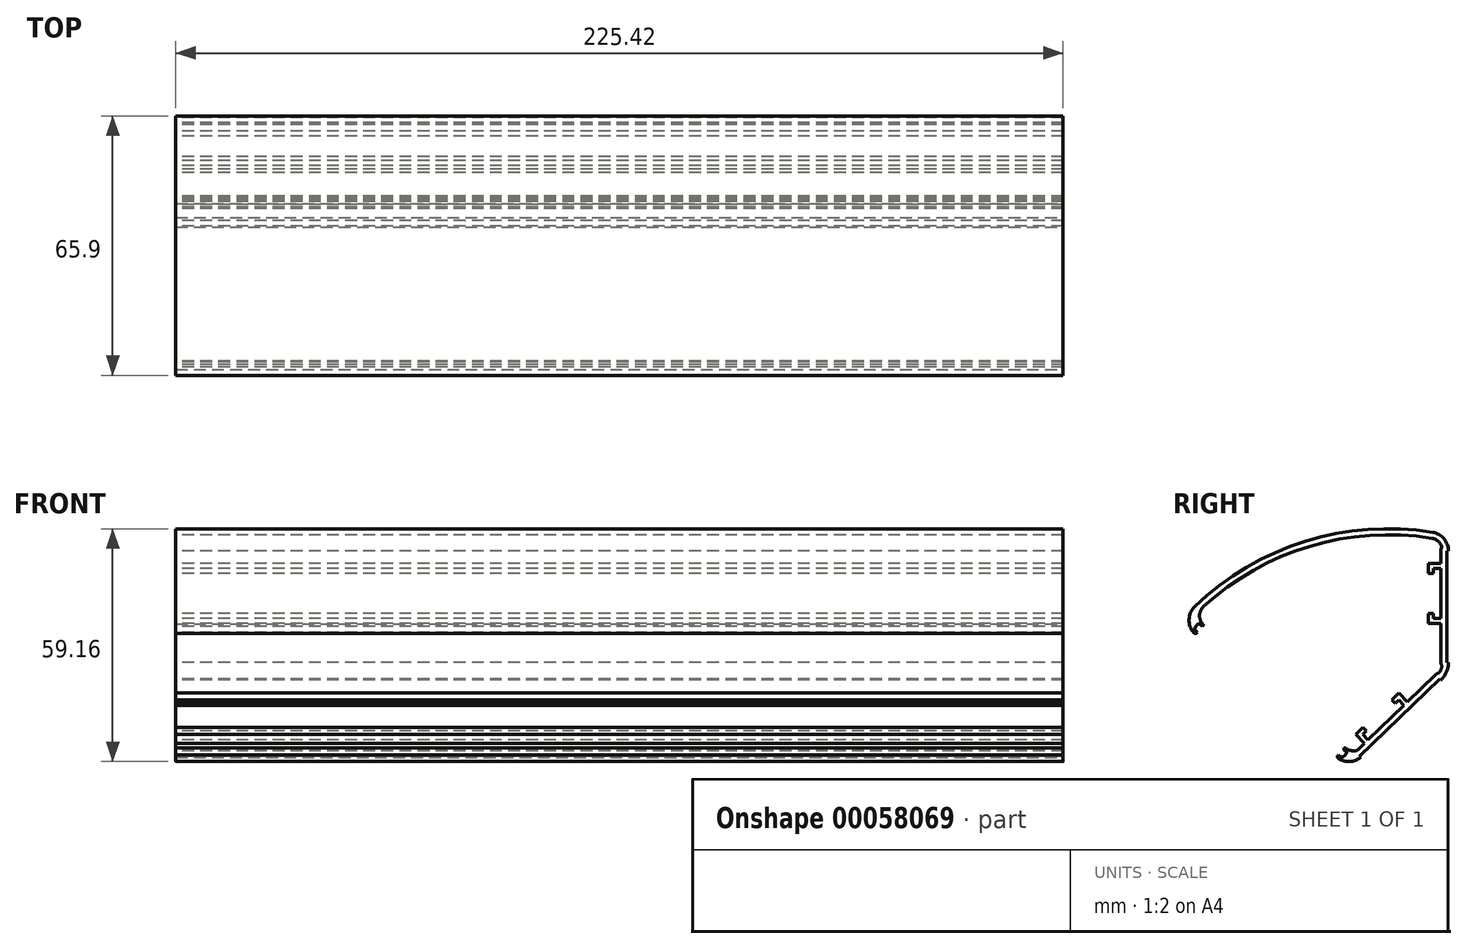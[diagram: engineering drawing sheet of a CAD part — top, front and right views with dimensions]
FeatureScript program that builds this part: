
annotation { "Feature Type Name" : "Feature", "Feature Type Description" : "" }
export const myFeature = defineFeature(function(context is Context, id is Id, definition is map)
    precondition{}
    {
        {
            var Q0;
            Q0=qCreatedBy(makeId("Right.planeOp"),FACE);
            var sketch = newSketch(context, id + "F0", { "sketchPlane" : qUnion([Q0])});
            skLineSegment(sketch, "E0", {"start": v(-25.12, -24.26) * mm, "end": v(0, 0) * mm});
            skLineSegment(sketch, "E1", {"start": v(0, 0) * mm, "end": v(0, 34.93) * mm});
            skArc(sketch, "E2", {"start": v(0, 34.92) * mm, "mid": v(-34.7, 33.87) * mm, "end": v(-64.76, 16.49) * mm});
            skLineSegment(sketch, "E3", {"start": v(-64.76, 16.49) * mm, "end": v(-68.18, 13.16) * mm});
            skLineSegment(sketch, "E4", {"start": v(-25.12, -24.26) * mm, "end": v(-68.18, 13.16) * mm});
            skLineSegment(sketch, "E5", {"start": v(-64.76, 16.49) * mm, "end": v(-25.12, -24.26) * mm, "construction": true});
            skLineSegment(sketch, "E6", {"start": v(-64.76, 16.49) * mm, "end": v(0, 34.93) * mm, "construction": true});
            skSolve(sketch);
        }
        {
            var Q0;
            Q0=qSketchRegion(id+"F0",true);
            extrude(context, id + "F1", {"entities" : qUnion([Q0]), "endBound" : BoundingType.SYMMETRIC, "depth" : 225.42 * mm});
        }
        {
            var Q0;
            Q0=makeQuery(id+"F1.opExtrude","SWEPT_EDGE",EDGE,{"disambiguationData":[OSD([sQuery(id+"F0.wireOp",EDGE,"E1"),sQuery(id+"F0.wireOp",EDGE,"E2")])]});
            var Q1;
            Q1=makeQuery(id+"F1.opExtrude","SWEPT_EDGE",EDGE,{"disambiguationData":[OSD([sQuery(id+"F0.wireOp",EDGE,"E0"),sQuery(id+"F0.wireOp",EDGE,"E4")])]});
            var Q2;
            Q2=makeQuery(id+"F1.opExtrude","SWEPT_EDGE",EDGE,{"disambiguationData":[OSD([sQuery(id+"F0.wireOp",EDGE,"E3"),sQuery(id+"F0.wireOp",EDGE,"E4")])]});
            fillet(context, id + "F2", {"entities" : qUnion([Q0, Q1, Q2]), "radius" : 4.76 * mm, "tangentPropagation" : true, "allowEdgeOverflow" : false});
        }
        {
            var Q0;
            Q0=makeQuery(id+"F1.opExtrude","SWEPT_EDGE",EDGE,{"disambiguationData":[OSD([sQuery(id+"F0.wireOp",EDGE,"E0"),sQuery(id+"F0.wireOp",EDGE,"E1")])]});
            fillet(context, id + "F3", {"entities" : qUnion([Q0]), "radius" : 6.35 * mm, "tangentPropagation" : true, "allowEdgeOverflow" : false});
        }
        {
            var Q0;
            Q0=makeQuery(id+"F1.opExtrude","CAP_FACE",FACE,{"disambiguationData":[OSD([sQuery(id+"F0.wireOp",EDGE,"E0"),sQuery(id+"F0.wireOp",EDGE,"E1"),sQuery(id+"F0.wireOp",EDGE,"E2"),sQuery(id+"F0.wireOp",EDGE,"E3"),sQuery(id+"F0.wireOp",EDGE,"E4")])],"isStart":true});
            var Q1;
            Q1=makeQuery(id+"F1.opExtrude","CAP_FACE",FACE,{"disambiguationData":[OSD([sQuery(id+"F0.wireOp",EDGE,"E0"),sQuery(id+"F0.wireOp",EDGE,"E1"),sQuery(id+"F0.wireOp",EDGE,"E2"),sQuery(id+"F0.wireOp",EDGE,"E3"),sQuery(id+"F0.wireOp",EDGE,"E4")])],"isStart":false});
            var Q2;
            Q2=makeQuery(id+"F1.opExtrude","SWEPT_FACE",FACE,{"disambiguationData":[OSD([sQuery(id+"F0.wireOp",EDGE,"E4")])]});
            shell(context, id + "F4", {"entities" : qUnion([Q0, Q1, Q2]), "thickness" : 1.52 * mm});
        }
        {
            var Q0;
            Q0=makeQuery(id+"F1.opExtrude","CAP_FACE",FACE,{"disambiguationData":[OSD([sQuery(id+"F0.wireOp",EDGE,"E0"),sQuery(id+"F0.wireOp",EDGE,"E1"),sQuery(id+"F0.wireOp",EDGE,"E2"),sQuery(id+"F0.wireOp",EDGE,"E3"),sQuery(id+"F0.wireOp",EDGE,"E4")])],"isStart":true});
            var sketch = newSketch(context, id + "F5", { "sketchPlane" : qUnion([Q0])});
            skLineSegment(sketch, "E7", {"start": v(63.27, 10.92) * mm, "end": v(62.18, 12.16) * mm});
            skArc(sketch, "E8.0", {"start": v(63.27, 10.92) * mm, "mid": v(64.38, 13.28) * mm, "end": v(63.39, 15.7) * mm});
            skArc(sketch, "E9", {"start": v(62.18, 12.16) * mm, "mid": v(63.23, 14.47) * mm, "end": v(62.22, 16.8) * mm});
            skSolve(sketch);
        }
        {
            var Q0;
            {var subQ0=sQuery(id+"F0.wireOp",EDGE,"E3");Q0=makeQuery(id+"FXWxfeTe23RxrKB_1.boolean.opBoolean","MERGE",FACE,{"derivedFrom":[makeQuery(id+"F1.opExtrude","CAP_FACE",FACE,{"disambiguationData":[OSD([sQuery(id+"F0.wireOp",EDGE,"E0"),sQuery(id+"F0.wireOp",EDGE,"E1"),sQuery(id+"F0.wireOp",EDGE,"E2"),subQ0,sQuery(id+"F0.wireOp",EDGE,"E4")])],"isStart":true}),makeQuery(id+"FXWxfeTe23RxrKB_1.opExtrude","CAP_FACE",FACE,{"disambiguationData":[OSD([subQ0,sQuery(id+"F5.wireOp",EDGE,"f8929549-29da-4568-b1ae-587f62ae2228.0"),sQuery(id+"F5.wireOp",EDGE,"E7"),sQuery(id+"F5.wireOp",EDGE,"b0cd2a88-d953-423b-8e6f-4eb86873c5e2")])],"isStart":true})]});}
            var sketch = newSketch(context, id + "F6", { "sketchPlane" : qUnion([Q0])});
            skArc(sketch, "E10.0", {"start": v(23.04, -20.13) * mm, "mid": v(25.2, -21.04) * mm, "end": v(27.42, -20.25) * mm});
            skLineSegment(sketch, "E11", {"start": v(27.42, -20.25) * mm, "end": v(26.33, -19) * mm});
            skArc(sketch, "E12", {"start": v(21.75, -18.88) * mm, "mid": v(24.02, -19.83) * mm, "end": v(26.33, -19) * mm});
            skLineSegment(sketch, "E13", {"start": v(26.33, -19) * mm, "end": v(24.2, -20.85) * mm, "construction": true});
            skSolve(sketch);
        }
        {
            var Q0;
            Q0=makeQuery(id+"F5.imprint","IMPRINT",FACE,{"disambiguationData":[TD([[makeQuery(id+"F5.imprint","IMPRINT",EDGE,{"derivedFrom":sQuery(id+"F5.wireOp",EDGE,"E7")}),-1.0]])]});
            var Q1;
            {var subQ0=sQuery(id+"F6.wireOp",EDGE,"E10.0");Q1=makeQuery(id+"F6.imprint","IMPRINT",FACE,{"disambiguationData":[TD([[makeQuery(id+"F6.imprint","IMPRINT",EDGE,{"derivedFrom":subQ0}),1.0]])]});}
            var Q2;
            Q2=makeQuery(id+"F1.opExtrude","CAP_FACE",FACE,{"disambiguationData":[OSD([sQuery(id+"F0.wireOp",EDGE,"E0"),sQuery(id+"F0.wireOp",EDGE,"E1"),sQuery(id+"F0.wireOp",EDGE,"E2"),sQuery(id+"F0.wireOp",EDGE,"E3"),sQuery(id+"F0.wireOp",EDGE,"E4")])],"isStart":false});
            extrude(context, id + "F7", {"entities" : qUnion([Q0, Q1]), "operationType" : NewBodyOperationType.ADD, "endBound" : BoundingType.UP_TO_SURFACE, "oppositeDirection" : true, "endBoundEntityFace" : qUnion([Q2]), "depth" : 25.4 * mm});
        }
        {
            var Q0;
            {var subQ0=sQuery(id+"F0.wireOp",EDGE,"E0");var subQ1=sQuery(id+"F0.wireOp",EDGE,"E2");Q0=makeQuery(id+"F7.boolean.opBoolean","MERGE",FACE,{"derivedFrom":[makeQuery(id+"F1.opExtrude","CAP_FACE",FACE,{"disambiguationData":[OSD([subQ0,sQuery(id+"F0.wireOp",EDGE,"E1"),subQ1,sQuery(id+"F0.wireOp",EDGE,"E3"),sQuery(id+"F0.wireOp",EDGE,"E4")])],"isStart":true}),makeQuery(id+"F7.opExtrude","CAP_FACE",FACE,{"disambiguationData":[OSD([subQ1,sQuery(id+"F5.wireOp",EDGE,"E7"),sQuery(id+"F5.wireOp",EDGE,"E8.0"),sQuery(id+"F5.wireOp",EDGE,"E9")])],"isStart":true}),makeQuery(id+"F7.opExtrude","CAP_FACE",FACE,{"disambiguationData":[OSD([subQ0,sQuery(id+"F6.wireOp",EDGE,"E10.0"),sQuery(id+"F6.wireOp",EDGE,"E11"),sQuery(id+"F6.wireOp",EDGE,"E12")])],"isStart":true})]});}
            var sketch = newSketch(context, id + "F8", { "sketchPlane" : qUnion([Q0])});
            skLineSegment(sketch, "E14", {"start": v(63.18, 11.01) * mm, "end": v(27.33, -20.15) * mm, "construction": true});
            skSolve(sketch);
        }
        {
            var Q0;
            {var subQ4=sQuery(id+"F0.wireOp",EDGE,"E0");var subQ12=makeQuery(id+"F1.opExtrude","CAP_EDGE",EDGE,{"disambiguationData":[OSD([subQ4])],"isStart":true});Q0=makeQuery(id+"F8.imprint","IMPRINT",FACE,{"disambiguationData":[TD([[makeQuery(id+"F8.imprint","IMPRINT",EDGE,{"derivedFrom":subQ12}),-1.0]])]});}
            var sketch = newSketch(context, id + "F9", { "sketchPlane" : qUnion([Q0])});
            skLineSegment(sketch, "E15", {"start": v(62.56, 11.73) * mm, "end": v(63.8, 10.3) * mm});
            skLineSegment(sketch, "E16", {"start": v(63.8, 10.3) * mm, "end": v(64.77, 11.13) * mm});
            skLineSegment(sketch, "E17", {"start": v(64.77, 11.13) * mm, "end": v(63.52, 12.56) * mm});
            skLineSegment(sketch, "E18", {"start": v(63.52, 12.56) * mm, "end": v(62.56, 11.73) * mm});
            skPoint(sketch, "E19", {"position": v(63.18, 11.01) * mm});
            skSolve(sketch);
        }
        {
            var Q0;
            {var subQ4=sQuery(id+"F0.wireOp",EDGE,"E0");var subQ12=makeQuery(id+"F1.opExtrude","CAP_EDGE",EDGE,{"disambiguationData":[OSD([subQ4])],"isStart":true});Q0=makeQuery(id+"F8.imprint","IMPRINT",FACE,{"disambiguationData":[TD([[makeQuery(id+"F8.imprint","IMPRINT",EDGE,{"derivedFrom":subQ12}),-1.0]])]});}
            var sketch = newSketch(context, id + "F10", { "sketchPlane" : qUnion([Q0])});
            skLineSegment(sketch, "E20", {"start": v(26.7, -19.43) * mm, "end": v(27.96, -20.87) * mm});
            skLineSegment(sketch, "E21", {"start": v(27.96, -20.87) * mm, "end": v(27, -21.7) * mm});
            skLineSegment(sketch, "E22", {"start": v(27, -21.7) * mm, "end": v(25.75, -20.27) * mm});
            skLineSegment(sketch, "E23", {"start": v(25.75, -20.27) * mm, "end": v(26.7, -19.43) * mm});
            skPoint(sketch, "E24", {"position": v(27.33, -20.15) * mm});
            skSolve(sketch);
        }
        {
            var Q0;
            Q0 = qSketchRegion(id + "F9", true);
            var Q1;
            Q1 = qSketchRegion(id + "F10", true);
            var Q2;
            {var subQ0=sQuery(id+"F0.wireOp",EDGE,"E0");var subQ1=sQuery(id+"F0.wireOp",EDGE,"E2");Q2=makeQuery(id+"F7.boolean.opBoolean","MERGE",FACE,{"derivedFrom":[makeQuery(id+"F1.opExtrude","CAP_FACE",FACE,{"disambiguationData":[OSD([subQ0,sQuery(id+"F0.wireOp",EDGE,"E1"),subQ1,sQuery(id+"F0.wireOp",EDGE,"E3"),sQuery(id+"F0.wireOp",EDGE,"E4")])],"isStart":false}),makeQuery(id+"F7.opExtrude","CAP_FACE",FACE,{"disambiguationData":[OSD([subQ1,sQuery(id+"F5.wireOp",EDGE,"E7"),sQuery(id+"F5.wireOp",EDGE,"E8.0"),sQuery(id+"F5.wireOp",EDGE,"E9")])],"isStart":false}),makeQuery(id+"F7.opExtrude","CAP_FACE",FACE,{"disambiguationData":[OSD([subQ0,sQuery(id+"F6.wireOp",EDGE,"E10.0"),sQuery(id+"F6.wireOp",EDGE,"E11"),sQuery(id+"F6.wireOp",EDGE,"E12")])],"isStart":false})]});}
            extrude(context, id + "F11", {"entities" : qUnion([Q0, Q1]), "operationType" : NewBodyOperationType.REMOVE, "endBound" : BoundingType.UP_TO_SURFACE, "oppositeDirection" : true, "endBoundEntityFace" : qUnion([Q2]), "depth" : 25.4 * mm});
        }
        {
            var Q0;
            Q0=makeQuery(id+"F11.boolean.opBoolean","COPY",EDGE,{"derivedFrom":makeQuery(id+"F11.opExtrude","SWEPT_EDGE",EDGE,{"disambiguationData":[OSD([sQuery(id+"F10.wireOp",EDGE,"E21"),sQuery(id+"F10.wireOp",EDGE,"E22")])]})});
            var Q1;
            Q1=makeQuery(id+"F11.boolean.opBoolean","COPY",EDGE,{"derivedFrom":makeQuery(id+"F11.opExtrude","SWEPT_EDGE",EDGE,{"disambiguationData":[OSD([sQuery(id+"F9.wireOp",EDGE,"E16"),sQuery(id+"F9.wireOp",EDGE,"E17")])]})});
            fillet(context, id + "F12", {"entities" : qUnion([Q0, Q1]), "radius" : 0.76 * mm, "tangentPropagation" : true, "allowEdgeOverflow" : false});
        }
        {
            var Q0;
            {var subQ0=sQuery(id+"F0.wireOp",EDGE,"E4");Q0=makeQuery(id+"F2.opFillet","BLEND_EDGE",EDGE,{"blendedFrom":[makeQuery(id+"F1.opExtrude","SWEPT_EDGE",EDGE,{"disambiguationData":[OSD([sQuery(id+"F0.wireOp",EDGE,"E3"),subQ0])]}),makeQuery(id+"F1.opExtrude","SWEPT_FACE",FACE,{"disambiguationData":[OSD([subQ0])]})],"blendedInto":[makeQuery(id+"F1.opExtrude","SWEPT_FACE",FACE,{"disambiguationData":[OSD([subQ0])]})]});}
            var Q1;
            {var subQ0=sQuery(id+"F0.wireOp",EDGE,"E4");Q1=makeQuery(id+"F2.opFillet","BLEND_EDGE",EDGE,{"blendedFrom":[makeQuery(id+"F1.opExtrude","SWEPT_EDGE",EDGE,{"disambiguationData":[OSD([sQuery(id+"F0.wireOp",EDGE,"E0"),subQ0])]}),makeQuery(id+"F1.opExtrude","SWEPT_FACE",FACE,{"disambiguationData":[OSD([subQ0])]})],"blendedInto":[makeQuery(id+"F1.opExtrude","SWEPT_FACE",FACE,{"disambiguationData":[OSD([subQ0])]})]});}
            fillet(context, id + "F13", {"entities" : qUnion([Q0, Q1]), "radius" : 0.5 * mm, "tangentPropagation" : true, "allowEdgeOverflow" : false});
        }
        {
            var Q0;
            Q0=makeQuery(id+"F11.boolean.opBoolean","COPY",EDGE,{"derivedFrom":makeQuery(id+"F11.opExtrude","SWEPT_EDGE",EDGE,{"disambiguationData":[OSD([sQuery(id+"F10.wireOp",EDGE,"E22"),sQuery(id+"F10.wireOp",EDGE,"E23")])]})});
            var Q1;
            Q1=makeQuery(id+"F11.boolean.opBoolean","COPY",EDGE,{"derivedFrom":makeQuery(id+"F11.opExtrude","SWEPT_EDGE",EDGE,{"disambiguationData":[OSD([sQuery(id+"F0.wireOp",EDGE,"E0"),sQuery(id+"F0.wireOp",EDGE,"E1"),sQuery(id+"F0.wireOp",EDGE,"E2"),sQuery(id+"F0.wireOp",EDGE,"E3"),sQuery(id+"F0.wireOp",EDGE,"E4"),sQuery(id+"F6.wireOp",EDGE,"E11"),sQuery(id+"F10.wireOp",EDGE,"E20"),sQuery(id+"F10.wireOp",EDGE,"E23")])]})});
            var Q2;
            Q2=makeQuery(id+"F7.opExtrude","SWEPT_EDGE",EDGE,{"disambiguationData":[OSD([sQuery(id+"F6.wireOp",EDGE,"E11"),sQuery(id+"F6.wireOp",EDGE,"E12")])]});
            var Q3;
            Q3=makeQuery(id+"F11.boolean.opBoolean","COPY",EDGE,{"derivedFrom":makeQuery(id+"F11.opExtrude","SWEPT_EDGE",EDGE,{"disambiguationData":[OSD([sQuery(id+"F0.wireOp",EDGE,"E0"),sQuery(id+"F0.wireOp",EDGE,"E1"),sQuery(id+"F0.wireOp",EDGE,"E2"),sQuery(id+"F0.wireOp",EDGE,"E3"),sQuery(id+"F0.wireOp",EDGE,"E4"),sQuery(id+"F5.wireOp",EDGE,"E7"),sQuery(id+"F9.wireOp",EDGE,"E15"),sQuery(id+"F9.wireOp",EDGE,"E18")])]})});
            var Q4;
            Q4=makeQuery(id+"F7.opExtrude","SWEPT_EDGE",EDGE,{"disambiguationData":[OSD([sQuery(id+"F5.wireOp",EDGE,"E7"),sQuery(id+"F5.wireOp",EDGE,"E9")])]});
            var Q5;
            Q5=makeQuery(id+"F11.boolean.opBoolean","COPY",EDGE,{"derivedFrom":makeQuery(id+"F11.opExtrude","SWEPT_EDGE",EDGE,{"disambiguationData":[OSD([sQuery(id+"F9.wireOp",EDGE,"E17"),sQuery(id+"F9.wireOp",EDGE,"E18")])]})});
            fillet(context, id + "F14", {"entities" : qUnion([Q0, Q1, Q2, Q3, Q4, Q5]), "radius" : 0.25 * mm, "tangentPropagation" : true, "allowEdgeOverflow" : false});
        }
        {
            var Q0;
            {var subQ2=sQuery(id+"F0.wireOp",EDGE,"E2");var subQ10=makeQuery(id+"F1.opExtrude","CAP_EDGE",EDGE,{"disambiguationData":[OSD([subQ2])],"isStart":true});Q0=makeQuery(id+"F8.imprint","IMPRINT",FACE,{"disambiguationData":[TD([[makeQuery(id+"F8.imprint","IMPRINT",EDGE,{"derivedFrom":subQ10}),-1.0]])]});}
            var sketch = newSketch(context, id + "F15", { "sketchPlane" : qUnion([Q0])});
            skLineSegment(sketch, "E25.0", {"start": v(0, 0) * mm, "end": v(0, 30.99) * mm, "construction": true});
            skLineSegment(sketch, "E25.1", {"start": v(21.98, -21.23) * mm, "end": v(0, 0) * mm, "construction": true});
            skLineSegment(sketch, "E26", {"start": v(0, 0) * mm, "end": v(1.9, 0.8) * mm, "construction": true});
            skSolve(sketch);
        }
        {
            var Q0;
            {var subQ2=sQuery(id+"F0.wireOp",EDGE,"E2");var subQ10=makeQuery(id+"F1.opExtrude","CAP_EDGE",EDGE,{"disambiguationData":[OSD([subQ2])],"isStart":true});Q0=makeQuery(id+"F8.imprint","IMPRINT",FACE,{"disambiguationData":[TD([[makeQuery(id+"F8.imprint","IMPRINT",EDGE,{"derivedFrom":subQ10}),-1.0]])]});}
            var sketch = newSketch(context, id + "F16", { "sketchPlane" : qUnion([Q0])});
            skLineSegment(sketch, "E27.bottom", {"start": v(0, 30.99) * mm, "end": v(0.4, 30.99) * mm});
            skLineSegment(sketch, "E27.top", {"start": v(0, 2.7) * mm, "end": v(0.4, 2.7) * mm});
            skLineSegment(sketch, "E27.left", {"start": v(0, 30.99) * mm, "end": v(0, 2.7) * mm});
            skLineSegment(sketch, "E27.right", {"start": v(0.4, 30.99) * mm, "end": v(0.4, 2.7) * mm});
            skLineSegment(sketch, "E28.MirrorCS", {"start": v(22.56, -21.24) * mm, "end": v(2.21, -1.59) * mm});
            skLineSegment(sketch, "E29.MirrorCS", {"start": v(1.94, -1.87) * mm, "end": v(2.21, -1.59) * mm});
            skLineSegment(sketch, "E30.MirrorCS", {"start": v(22.29, -21.52) * mm, "end": v(1.94, -1.87) * mm});
            skLineSegment(sketch, "E31.MirrorCS", {"start": v(22.29, -21.52) * mm, "end": v(22.56, -21.24) * mm});
            skSolve(sketch);
        }
        {
            var Q0;
            Q0 = qSketchRegion(id + "F16", true);
            var Q1;
            {var subQ0=sQuery(id+"F0.wireOp",EDGE,"E0");var subQ1=sQuery(id+"F0.wireOp",EDGE,"E2");Q1=makeQuery(id+"F7.boolean.opBoolean","MERGE",FACE,{"derivedFrom":[makeQuery(id+"F1.opExtrude","CAP_FACE",FACE,{"disambiguationData":[OSD([subQ0,sQuery(id+"F0.wireOp",EDGE,"E1"),subQ1,sQuery(id+"F0.wireOp",EDGE,"E3"),sQuery(id+"F0.wireOp",EDGE,"E4")])],"isStart":false}),makeQuery(id+"F7.opExtrude","CAP_FACE",FACE,{"disambiguationData":[OSD([subQ1,sQuery(id+"F5.wireOp",EDGE,"E7"),sQuery(id+"F5.wireOp",EDGE,"E8.0"),sQuery(id+"F5.wireOp",EDGE,"E9")])],"isStart":false}),makeQuery(id+"F7.opExtrude","CAP_FACE",FACE,{"disambiguationData":[OSD([subQ0,sQuery(id+"F6.wireOp",EDGE,"E10.0"),sQuery(id+"F6.wireOp",EDGE,"E11"),sQuery(id+"F6.wireOp",EDGE,"E12")])],"isStart":false})]});}
            extrude(context, id + "F17", {"entities" : qUnion([Q0]), "operationType" : NewBodyOperationType.REMOVE, "endBound" : BoundingType.UP_TO_SURFACE, "oppositeDirection" : true, "endBoundEntityFace" : qUnion([Q1]), "depth" : 25.4 * mm});
        }
        {
            var Q0;
            {var subQ2=sQuery(id+"F0.wireOp",EDGE,"E2");var subQ10=makeQuery(id+"F1.opExtrude","CAP_EDGE",EDGE,{"disambiguationData":[OSD([subQ2])],"isStart":true});Q0=makeQuery(id+"F8.imprint","IMPRINT",FACE,{"disambiguationData":[TD([[makeQuery(id+"F8.imprint","IMPRINT",EDGE,{"derivedFrom":subQ10}),-1.0]])]});}
            var sketch = newSketch(context, id + "F18", { "sketchPlane" : qUnion([Q0])});
            skLineSegment(sketch, "E32.left", {"start": v(1.52, 30.99) * mm, "end": v(1.52, 2.7) * mm});
            skLineSegment(sketch, "E32.right", {"start": v(1.92, 30.99) * mm, "end": v(1.92, 2.7) * mm});
            skArc(sketch, "E33", {"start": v(1.92, 30.99) * mm, "mid": v(1.88, 31.4) * mm, "end": v(1.76, 31.78) * mm});
            skArc(sketch, "E34", {"start": v(1.76, 31.78) * mm, "mid": v(1.71, 31.98) * mm, "end": v(1.75, 32.18) * mm});
            skArc(sketch, "E35", {"start": v(1.52, 30.99) * mm, "mid": v(1.58, 31.6) * mm, "end": v(1.75, 32.18) * mm});
            skArc(sketch, "E36", {"start": v(1.52, 2.7) * mm, "mid": v(1.56, 2.1) * mm, "end": v(1.67, 1.5) * mm});
            skArc(sketch, "E37", {"start": v(1.92, 2.7) * mm, "mid": v(1.87, 2.29) * mm, "end": v(1.72, 1.9) * mm});
            skArc(sketch, "E38", {"start": v(1.72, 1.9) * mm, "mid": v(1.66, 1.7) * mm, "end": v(1.67, 1.5) * mm});
            skLineSegment(sketch, "E39.MirrorCS", {"start": v(23.62, -20.14) * mm, "end": v(3.27, -0.5) * mm});
            skArc(sketch, "E40.MirrorCS", {"start": v(3.27, -0.5) * mm, "mid": v(2.94, -0.24) * mm, "end": v(2.56, -0.08) * mm});
            skArc(sketch, "E41.MirrorCS", {"start": v(2.56, -0.08) * mm, "mid": v(2.38, 0) * mm, "end": v(2.24, 0.16) * mm});
            skArc(sketch, "E42.MirrorCS", {"start": v(3, -0.78) * mm, "mid": v(2.6, -0.33) * mm, "end": v(2.24, 0.16) * mm});
            skLineSegment(sketch, "E43.MirrorCS", {"start": v(23.35, -20.43) * mm, "end": v(3, -0.78) * mm});
            skArc(sketch, "E44.MirrorCS", {"start": v(23.62, -20.14) * mm, "mid": v(23.89, -20.45) * mm, "end": v(24.08, -20.81) * mm});
            skArc(sketch, "E45.MirrorCS", {"start": v(24.08, -20.81) * mm, "mid": v(24.2, -20.98) * mm, "end": v(24.36, -21.1) * mm});
            skArc(sketch, "E46.MirrorCS", {"start": v(23.35, -20.43) * mm, "mid": v(23.82, -20.8) * mm, "end": v(24.36, -21.1) * mm});
            skSolve(sketch);
        }
        {
            var Q0;
            Q0 = qSketchRegion(id + "F18", true);
            var Q1;
            {var subQ0=sQuery(id+"F0.wireOp",EDGE,"E0");var subQ1=sQuery(id+"F0.wireOp",EDGE,"E2");Q1=makeQuery(id+"F7.boolean.opBoolean","MERGE",FACE,{"derivedFrom":[makeQuery(id+"F1.opExtrude","CAP_FACE",FACE,{"disambiguationData":[OSD([subQ0,sQuery(id+"F0.wireOp",EDGE,"E1"),subQ1,sQuery(id+"F0.wireOp",EDGE,"E3"),sQuery(id+"F0.wireOp",EDGE,"E4")])],"isStart":false}),makeQuery(id+"F7.opExtrude","CAP_FACE",FACE,{"disambiguationData":[OSD([subQ1,sQuery(id+"F5.wireOp",EDGE,"E7"),sQuery(id+"F5.wireOp",EDGE,"E8.0"),sQuery(id+"F5.wireOp",EDGE,"E9")])],"isStart":false}),makeQuery(id+"F7.opExtrude","CAP_FACE",FACE,{"disambiguationData":[OSD([subQ0,sQuery(id+"F6.wireOp",EDGE,"E10.0"),sQuery(id+"F6.wireOp",EDGE,"E11"),sQuery(id+"F6.wireOp",EDGE,"E12")])],"isStart":false})]});}
            extrude(context, id + "F19", {"entities" : qUnion([Q0]), "operationType" : NewBodyOperationType.ADD, "endBound" : BoundingType.UP_TO_SURFACE, "oppositeDirection" : true, "endBoundEntityFace" : qUnion([Q1]), "depth" : 25.4 * mm});
        }
        {
            var Q0;
            {var subQ2=sQuery(id+"F0.wireOp",EDGE,"E2");var subQ10=makeQuery(id+"F1.opExtrude","CAP_EDGE",EDGE,{"disambiguationData":[OSD([subQ2])],"isStart":true});Q0=makeQuery(id+"F8.imprint","IMPRINT",FACE,{"disambiguationData":[TD([[makeQuery(id+"F8.imprint","IMPRINT",EDGE,{"derivedFrom":subQ10}),-1.0]])]});}
            var sketch = newSketch(context, id + "F20", { "sketchPlane" : qUnion([Q0])});
            skLineSegment(sketch, "E47", {"start": v(21.34, -17.94) * mm, "end": v(23.55, -15.65) * mm});
            skLineSegment(sketch, "E48", {"start": v(23.55, -15.65) * mm, "end": v(21.72, -13.89) * mm});
            skLineSegment(sketch, "E49", {"start": v(21.72, -13.89) * mm, "end": v(20.84, -14.8) * mm});
            skLineSegment(sketch, "E50", {"start": v(20.84, -14.8) * mm, "end": v(21.75, -15.68) * mm});
            skLineSegment(sketch, "E51", {"start": v(21.75, -15.68) * mm, "end": v(20.43, -17.05) * mm});
            skLineSegment(sketch, "E52", {"start": v(20.43, -17.05) * mm, "end": v(21.34, -17.94) * mm});
            skLineSegment(sketch, "E53", {"start": v(15.86, -12.64) * mm, "end": v(18.06, -10.36) * mm, "construction": true});
            skLineSegment(sketch, "E54.MirrorCS", {"start": v(13.53, -7.74) * mm, "end": v(12.61, -6.86) * mm});
            skLineSegment(sketch, "E55.MirrorCS", {"start": v(14.4, -6.83) * mm, "end": v(13.53, -7.74) * mm});
            skLineSegment(sketch, "E56.MirrorCS", {"start": v(12.58, -5.07) * mm, "end": v(14.4, -6.83) * mm});
            skLineSegment(sketch, "E57.MirrorCS", {"start": v(10.38, -7.35) * mm, "end": v(12.58, -5.07) * mm});
            skLineSegment(sketch, "E58.MirrorCS", {"start": v(11.3, -8.23) * mm, "end": v(10.38, -7.35) * mm});
            skLineSegment(sketch, "E59.MirrorCS", {"start": v(12.61, -6.86) * mm, "end": v(11.3, -8.23) * mm});
            skLineSegment(sketch, "E60.MirrorCS", {"start": v(5.1, 12.57) * mm, "end": v(5.1, 15.11) * mm});
            skLineSegment(sketch, "E61.MirrorCS", {"start": v(1.92, 12.57) * mm, "end": v(5.1, 12.57) * mm});
            skLineSegment(sketch, "E62.MirrorCS", {"start": v(1.92, 13.84) * mm, "end": v(1.92, 12.57) * mm});
            skLineSegment(sketch, "E63.MirrorCS", {"start": v(3.83, 13.84) * mm, "end": v(1.92, 13.84) * mm});
            skLineSegment(sketch, "E64.MirrorCS", {"start": v(3.83, 15.11) * mm, "end": v(3.83, 13.84) * mm});
            skLineSegment(sketch, "E65.MirrorCS", {"start": v(5.1, 15.11) * mm, "end": v(3.83, 15.11) * mm});
            skLineSegment(sketch, "E66.MirrorCS", {"start": v(5.1, 25.27) * mm, "end": v(3.83, 25.27) * mm});
            skLineSegment(sketch, "E67.MirrorCS", {"start": v(3.83, 25.27) * mm, "end": v(3.83, 26.54) * mm});
            skLineSegment(sketch, "E68.MirrorCS", {"start": v(5.1, 27.81) * mm, "end": v(5.1, 25.27) * mm});
            skLineSegment(sketch, "E69.MirrorCS", {"start": v(1.92, 27.81) * mm, "end": v(5.1, 27.81) * mm});
            skLineSegment(sketch, "E70.MirrorCS", {"start": v(1.92, 26.54) * mm, "end": v(1.92, 27.81) * mm});
            skLineSegment(sketch, "E71.MirrorCS", {"start": v(3.83, 26.54) * mm, "end": v(1.92, 26.54) * mm});
            skSolve(sketch);
        }
        {
            var Q0;
            Q0=makeQuery(id+"F20.imprint","IMPRINT",FACE,{"disambiguationData":[TD([[makeQuery(id+"F20.imprint","IMPRINT",EDGE,{"derivedFrom":sQuery(id+"F20.wireOp",EDGE,"E47")}),1.0]])]});
            var Q1;
            Q1=makeQuery(id+"F20.imprint","IMPRINT",FACE,{"disambiguationData":[TD([[makeQuery(id+"F20.imprint","IMPRINT",EDGE,{"derivedFrom":sQuery(id+"F20.wireOp",EDGE,"E54.MirrorCS")}),-1.0]])]});
            var Q2;
            Q2=makeQuery(id+"F20.imprint","IMPRINT",FACE,{"disambiguationData":[TD([[makeQuery(id+"F20.imprint","IMPRINT",EDGE,{"derivedFrom":sQuery(id+"F20.wireOp",EDGE,"E66.MirrorCS")}),-1.0]])]});
            var Q3;
            Q3=makeQuery(id+"F20.imprint","IMPRINT",FACE,{"disambiguationData":[TD([[makeQuery(id+"F20.imprint","IMPRINT",EDGE,{"derivedFrom":sQuery(id+"F20.wireOp",EDGE,"E60.MirrorCS")}),1.0]])]});
            var Q4;
            {var subQ0=sQuery(id+"F0.wireOp",EDGE,"E0");var subQ1=sQuery(id+"F0.wireOp",EDGE,"E2");Q4=makeQuery(id+"F19.boolean.opBoolean","MERGE",FACE,{"derivedFrom":[makeQuery(id+"F7.boolean.opBoolean","MERGE",FACE,{"derivedFrom":[makeQuery(id+"F1.opExtrude","CAP_FACE",FACE,{"disambiguationData":[OSD([subQ0,sQuery(id+"F0.wireOp",EDGE,"E1"),subQ1,sQuery(id+"F0.wireOp",EDGE,"E3"),sQuery(id+"F0.wireOp",EDGE,"E4")])],"isStart":false}),makeQuery(id+"F7.opExtrude","CAP_FACE",FACE,{"disambiguationData":[OSD([subQ1,sQuery(id+"F5.wireOp",EDGE,"E7"),sQuery(id+"F5.wireOp",EDGE,"E8.0"),sQuery(id+"F5.wireOp",EDGE,"E9")])],"isStart":false}),makeQuery(id+"F7.opExtrude","CAP_FACE",FACE,{"disambiguationData":[OSD([subQ0,sQuery(id+"F6.wireOp",EDGE,"E10.0"),sQuery(id+"F6.wireOp",EDGE,"E11"),sQuery(id+"F6.wireOp",EDGE,"E12")])],"isStart":false})]}),makeQuery(id+"F19.opExtrude","CAP_FACE",FACE,{"disambiguationData":[OSD([sQuery(id+"F18.wireOp",EDGE,"E32.left"),sQuery(id+"F18.wireOp",EDGE,"E32.right"),sQuery(id+"F18.wireOp",EDGE,"E33"),sQuery(id+"F18.wireOp",EDGE,"E34"),sQuery(id+"F18.wireOp",EDGE,"E35"),sQuery(id+"F18.wireOp",EDGE,"E36"),sQuery(id+"F18.wireOp",EDGE,"E37"),sQuery(id+"F18.wireOp",EDGE,"E38")])],"isStart":false}),makeQuery(id+"F19.opExtrude","CAP_FACE",FACE,{"disambiguationData":[OSD([sQuery(id+"F18.wireOp",EDGE,"E39.MirrorCS"),sQuery(id+"F18.wireOp",EDGE,"E40.MirrorCS"),sQuery(id+"F18.wireOp",EDGE,"E41.MirrorCS"),sQuery(id+"F18.wireOp",EDGE,"E42.MirrorCS"),sQuery(id+"F18.wireOp",EDGE,"E43.MirrorCS"),sQuery(id+"F18.wireOp",EDGE,"E44.MirrorCS"),sQuery(id+"F18.wireOp",EDGE,"E45.MirrorCS"),sQuery(id+"F18.wireOp",EDGE,"E46.MirrorCS")])],"isStart":false})]});}
            extrude(context, id + "F21", {"entities" : qUnion([Q0, Q1, Q2, Q3]), "operationType" : NewBodyOperationType.ADD, "endBound" : BoundingType.UP_TO_SURFACE, "oppositeDirection" : true, "endBoundEntityFace" : qUnion([Q4]), "depth" : 25.4 * mm});
        }
    });
